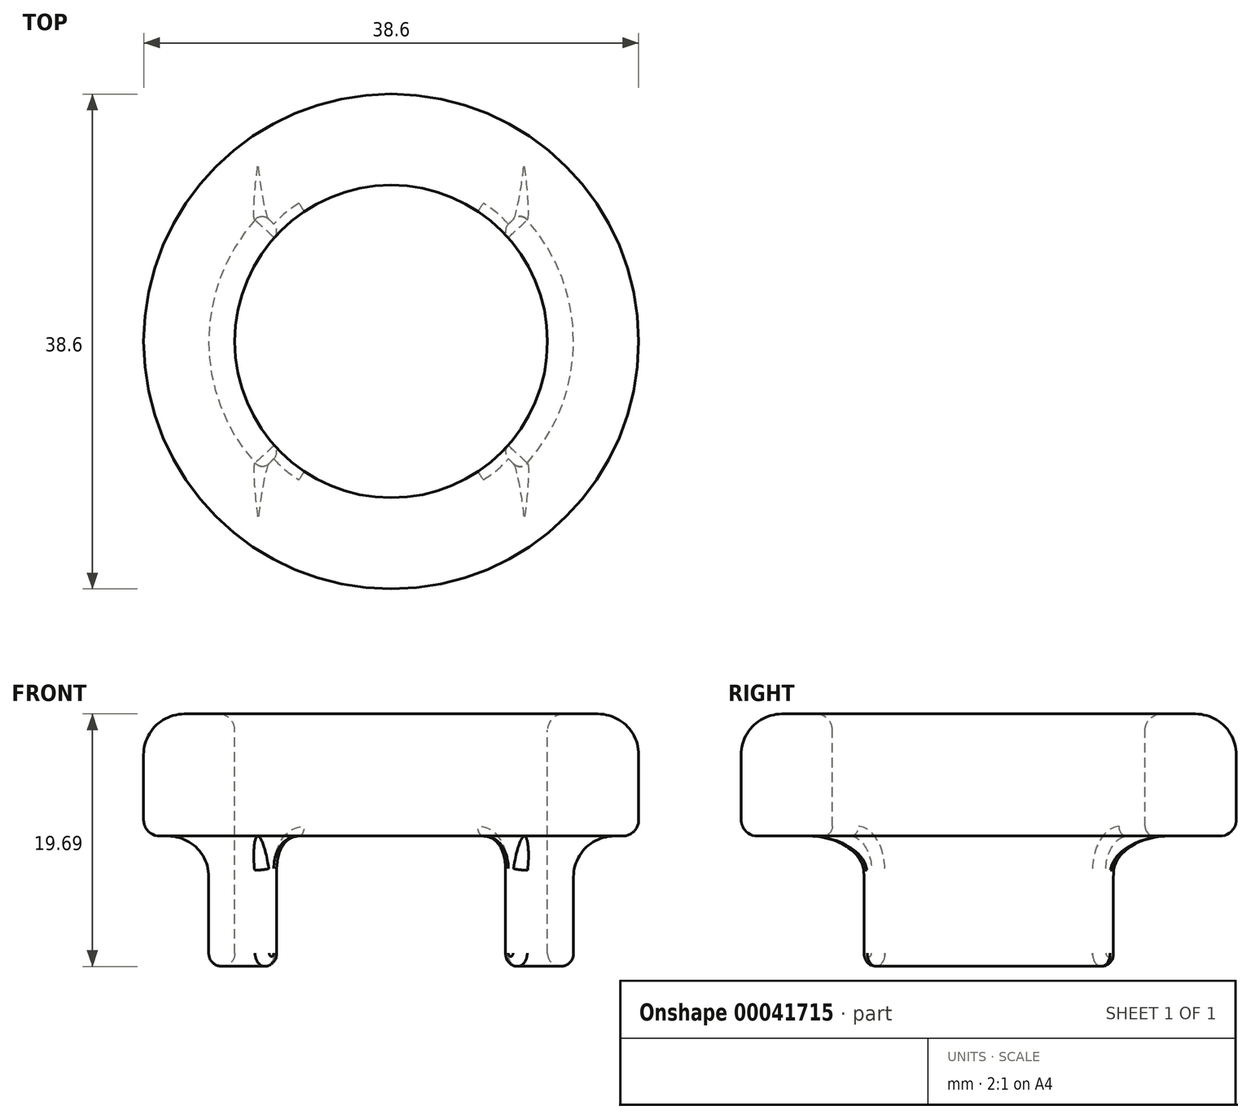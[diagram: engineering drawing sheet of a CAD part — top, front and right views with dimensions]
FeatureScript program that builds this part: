
annotation { "Feature Type Name" : "Feature", "Feature Type Description" : "" }
export const myFeature = defineFeature(function(context is Context, id is Id, definition is map)
    precondition{}
    {
        {
            var Q0;
            Q0=qCreatedBy(makeId("Front.planeOp"),FACE);
            var sketch = newSketch(context, id + "F0", { "sketchPlane" : qUnion([Q0])});
            skLineSegment(sketch, "E0", {"start": v(12.2, -18.67) * mm, "end": v(12.2, -1.27) * mm});
            skLineSegment(sketch, "E1", {"start": v(13.46, 0) * mm, "end": v(16.13, 0) * mm});
            skLineSegment(sketch, "E2", {"start": v(19.3, -3.17) * mm, "end": v(19.3, -8.26) * mm});
            skLineSegment(sketch, "E3", {"start": v(18.03, -9.53) * mm, "end": v(17.4, -9.53) * mm});
            skLineSegment(sketch, "E4", {"start": v(14.22, -12.7) * mm, "end": v(14.22, -18.67) * mm});
            skPoint(sketch, "E5.visualSharp", {"position": v(12.2, 0) * mm});
            skArc(sketch, "E5.filletArc", {"start": v(13.46, 0) * mm, "mid": v(12.56, -0.37) * mm, "end": v(12.2, -1.27) * mm});
            skPoint(sketch, "E6.visualSharp", {"position": v(19.3, 0) * mm});
            skArc(sketch, "E6.filletArc", {"start": v(19.3, -3.17) * mm, "mid": v(18.37, -0.93) * mm, "end": v(16.13, 0) * mm});
            skLineSegment(sketch, "E7", {"start": v(0, 0) * mm, "end": v(0, -18.67) * mm, "construction": true});
            skPoint(sketch, "E8.visualSharp", {"position": v(19.3, -9.53) * mm});
            skArc(sketch, "E8.filletArc", {"start": v(18.03, -9.53) * mm, "mid": v(18.93, -9.15) * mm, "end": v(19.3, -8.26) * mm});
            skPoint(sketch, "E9.visualSharp", {"position": v(14.22, -9.53) * mm});
            skArc(sketch, "E9.filletArc", {"start": v(17.4, -9.53) * mm, "mid": v(15.15, -10.45) * mm, "end": v(14.22, -12.7) * mm});
            skArc(sketch, "E10", {"start": v(14.22, -18.67) * mm, "mid": v(13.2, -19.69) * mm, "end": v(12.2, -18.67) * mm});
            skSolve(sketch);
        }
        {
            var Q0;
            Q0 = qSketchRegion(id + "F0", true);
            var Q1;
            Q1=sQuery(id+"F0.wireOp",EDGE,"E7");
            revolve(context, id + "F1", {"entities" : qUnion([Q0]), "axis" : qUnion([Q1]), "revolveType" : RevolveType.FULL});
        }
        {
            var Q0;
            Q0=makeQuery(id+"F1.opRevolve","SWEPT_FACE",FACE,{"disambiguationData":[OSD([sQuery(id+"F0.wireOp",EDGE,"E3")])]});
            var sketch = newSketch(context, id + "F2", { "sketchPlane" : qUnion([Q0])});
            skLineSegment(sketch, "E11", {"start": v(-17.96, -17.96) * mm, "end": v(0, 0) * mm});
            skLineSegment(sketch, "E12", {"start": v(0, 0) * mm, "end": v(17.96, -17.96) * mm});
            skArc(sketch, "E13", {"start": v(-17.96, -17.96) * mm, "mid": v(0, -25.4) * mm, "end": v(17.96, -17.96) * mm});
            skLineSegment(sketch, "E14.MirrorCS", {"start": v(-17.96, 17.96) * mm, "end": v(0, 0) * mm});
            skLineSegment(sketch, "E15.MirrorCS", {"start": v(0, 0) * mm, "end": v(17.96, 17.96) * mm});
            skArc(sketch, "E16.MirrorCS", {"start": v(-17.96, 17.96) * mm, "mid": v(0, 25.4) * mm, "end": v(17.96, 17.96) * mm});
            skSolve(sketch);
        }
        {
            var Q0;
            Q0 = qSketchRegion(id + "F2", true);
            extrude(context, id + "F3", {"entities" : qUnion([Q0]), "operationType" : NewBodyOperationType.REMOVE, "endBound" : BoundingType.THROUGH_ALL, "depth" : 25.4 * mm});
        }
        {
            var Q0;
            Q0=makeQuery(id+"F3.boolean.opBoolean","COPY",EDGE,{"derivedFrom":makeQuery(id+"F3.opExtrude","CAP_EDGE",EDGE,{"disambiguationData":[OSD([sQuery(id+"F2.wireOp",EDGE,"E11")])],"isStart":true})});
            var Q1;
            Q1=makeQuery(id+"F3.boolean.opBoolean","COPY",EDGE,{"derivedFrom":makeQuery(id+"F3.opExtrude","CAP_EDGE",EDGE,{"disambiguationData":[OSD([sQuery(id+"F2.wireOp",EDGE,"E14.MirrorCS")])],"isStart":true})});
            var Q2;
            Q2=makeQuery(id+"F3.boolean.opBoolean","COPY",EDGE,{"derivedFrom":makeQuery(id+"F3.opExtrude","CAP_EDGE",EDGE,{"disambiguationData":[OSD([sQuery(id+"F2.wireOp",EDGE,"E15.MirrorCS")])],"isStart":true})});
            var Q3;
            Q3=makeQuery(id+"F3.boolean.opBoolean","COPY",EDGE,{"derivedFrom":makeQuery(id+"F3.opExtrude","CAP_EDGE",EDGE,{"disambiguationData":[OSD([sQuery(id+"F2.wireOp",EDGE,"E12")])],"isStart":true})});
            fillet(context, id + "F4", {"entities" : qUnion([Q0, Q1, Q2, Q3]), "radius" : 2.54 * mm, "tangentPropagation" : true, "allowEdgeOverflow" : false});
        }
        {
            var Q0;
            Q0=makeQuery(id+"F3.boolean.opBoolean","INTERSECT",EDGE,{"derivedFrom":[makeQuery(id+"F1.opRevolve","SWEPT_FACE",FACE,{"disambiguationData":[OSD([sQuery(id+"F0.wireOp",EDGE,"E0")])]}),makeQuery(id+"F3.opExtrude","SWEPT_FACE",FACE,{"disambiguationData":[OSD([sQuery(id+"F2.wireOp",EDGE,"E12")])]})]});
            var Q1;
            Q1=makeQuery(id+"F3.boolean.opBoolean","INTERSECT",EDGE,{"derivedFrom":[makeQuery(id+"F1.opRevolve","SWEPT_FACE",FACE,{"disambiguationData":[OSD([sQuery(id+"F0.wireOp",EDGE,"E0")])]}),makeQuery(id+"F3.opExtrude","SWEPT_FACE",FACE,{"disambiguationData":[OSD([sQuery(id+"F2.wireOp",EDGE,"E15.MirrorCS")])]})]});
            fillet(context, id + "F5", {"entities" : qUnion([Q0, Q1]), "radius" : 0.76 * mm, "tangentPropagation" : true, "allowEdgeOverflow" : false});
        }
    });
